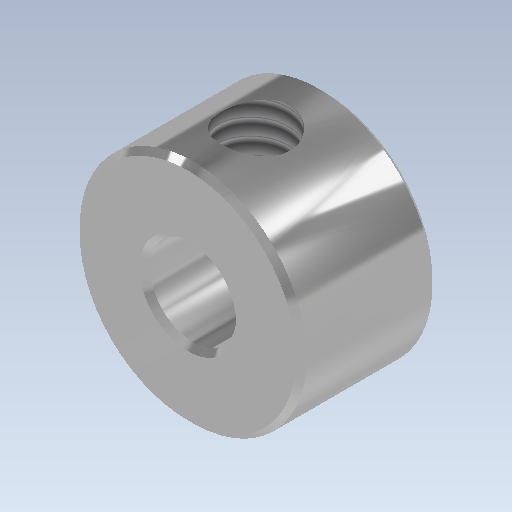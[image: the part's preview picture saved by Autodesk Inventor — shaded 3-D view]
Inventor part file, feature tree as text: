
AUTODESK INVENTOR PART (.ipt)
format: ipt  version: 2020 (Build 240168000, 168)  size: 146,944 bytes
history: native  units: in
note: dims shown in document units (in); Inventor stores cm internally (conversion verified against a paired STEP export)
features: sketch x3, chamfer x2, hole x2, extrude x1, plane x1
ambient origin geometry x8: Origin, YZ Plane, XZ Plane, XY Plane, X Axis, Y Axis, Z Axis, Center Point
bodies: Solid1 (feature_tree)
feature tree (9):
  extrude  "Extrusion1"  Depth=0.26in TaperAngle=0.0deg
  chamfer  "Chamfer1"  Distance=0.01in Angle=45.0deg
  hole  "Hole1"  [1 undecoded]
  plane  "Work Plane1"
  hole  "Hole2"  [1 undecoded]
  chamfer  "Chamfer2"  [1 undecoded]
  sketch  "Sketch1"  dims[d0=0.433in d1=0.26in d2=0.0in d3=0.01in d4=0.125in d5=45.0deg]
  sketch  "Sketch2"  dims[d6=0.165in d7=0.75in d8=0.375in d9=0.25in d10=0.5635in d11=1.0in d12=0.8108in]
  sketch  "Sketch3"  dims[d13=0.13in d14=0.75in d15=0.375in d16=0.25in d17=0.5635in d18=1.0in d19=0.8108in d20=0.01in d21=0.125in d22=45.0deg]
note: 3 required parameter values undecoded (feature->parameter linkage not recoverable at this tier; creation-order binding heuristic only, values carry confidence <= 0.55)
